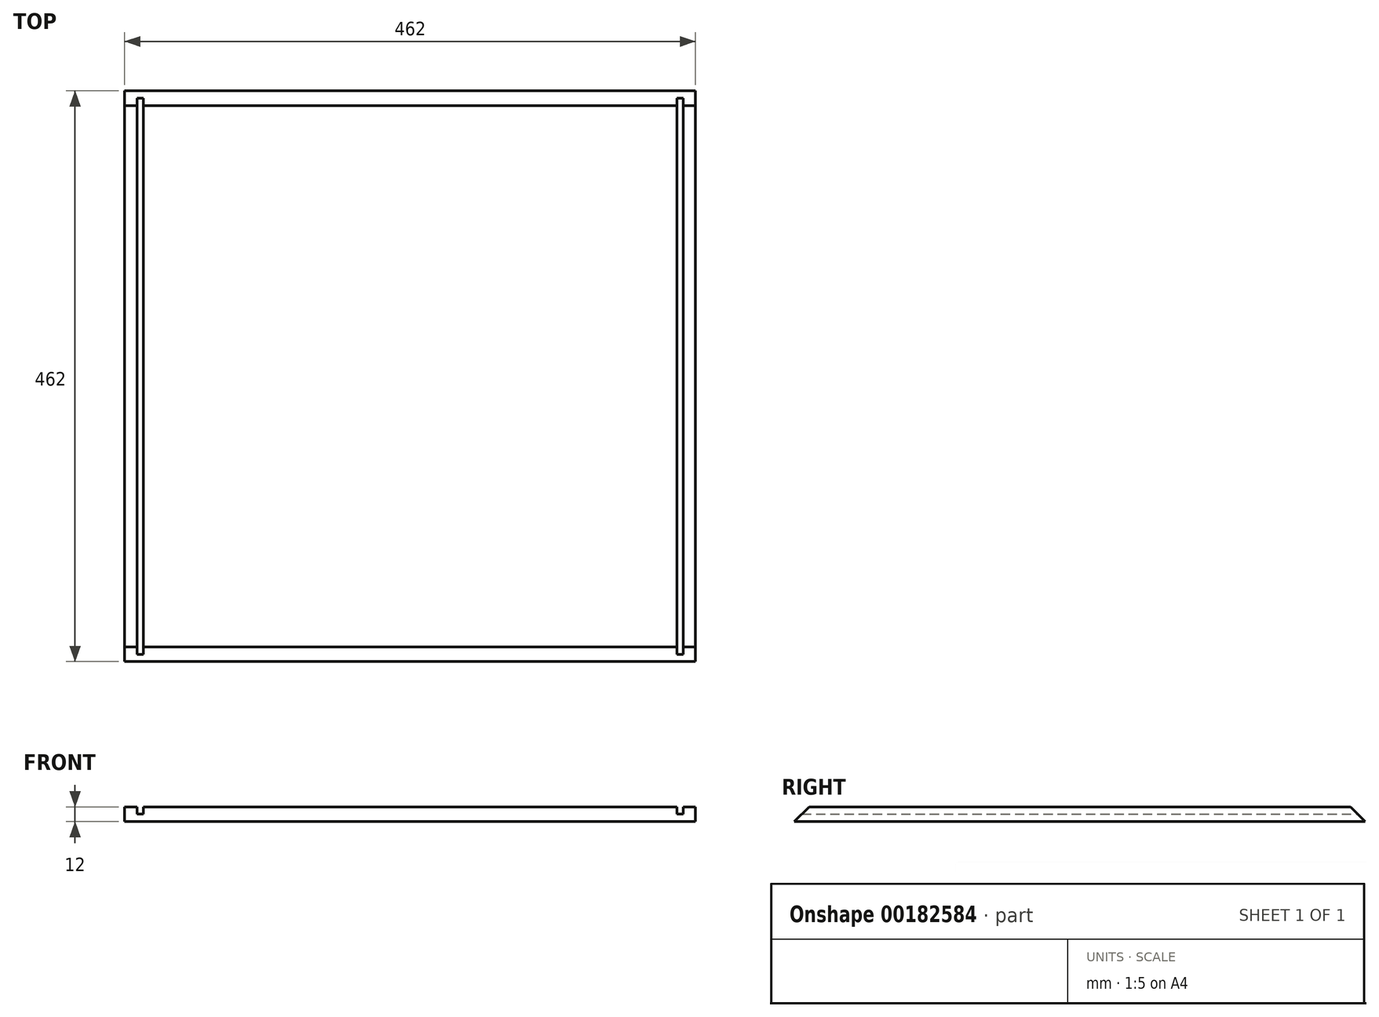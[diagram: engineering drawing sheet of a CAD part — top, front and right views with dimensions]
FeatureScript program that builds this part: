
annotation { "Feature Type Name" : "Feature", "Feature Type Description" : "" }
export const myFeature = defineFeature(function(context is Context, id is Id, definition is map)
    precondition{}
    {
        {
            var Q0;
            Q0=qCreatedBy(makeId("Top.planeOp"),FACE);
            var sketch = newSketch(context, id + "F0", { "sketchPlane" : qUnion([Q0])});
            skLineSegment(sketch, "E0.bottom", {"start": v(0, 0) * mm, "end": v(462, 0) * mm});
            skLineSegment(sketch, "E0.top", {"start": v(0, 462) * mm, "end": v(462, 462) * mm});
            skLineSegment(sketch, "E0.left", {"start": v(0, 0) * mm, "end": v(0, 462) * mm});
            skLineSegment(sketch, "E0.right", {"start": v(462, 0) * mm, "end": v(462, 462) * mm});
            skSolve(sketch);
        }
        {
            var Q0;
            Q0=qSketchRegion(id+"F0",true);
            extrude(context, id + "F1", {"entities" : qUnion([Q0]), "depth" : 12 * mm});
        }
        {
            var Q0;
            Q0=makeQuery(id+"F1.opExtrude","SWEPT_FACE",FACE,{"disambiguationData":[OSD([sQuery(id+"F0.wireOp",EDGE,"E0.right")])]});
            var sketch = newSketch(context, id + "F2", { "sketchPlane" : qUnion([Q0])});
            skLineSegment(sketch, "E1", {"start": v(0, 0) * mm, "end": v(231, 231) * mm});
            skLineSegment(sketch, "E2", {"start": v(231, 231) * mm, "end": v(462, 0) * mm});
            skLineSegment(sketch, "E3", {"start": v(462, 0) * mm, "end": v(539.72, 0) * mm});
            skLineSegment(sketch, "E4", {"start": v(539.72, 0) * mm, "end": v(539.72, 302.5) * mm});
            skLineSegment(sketch, "E5", {"start": v(539.72, 302.5) * mm, "end": v(-42.3, 283.65) * mm});
            skLineSegment(sketch, "E6", {"start": v(-42.3, 283.65) * mm, "end": v(-33.1, 0) * mm});
            skLineSegment(sketch, "E7", {"start": v(-33.1, 0) * mm, "end": v(0, 0) * mm});
            skSolve(sketch);
        }
        {
            var Q0;
            Q0=qSketchRegion(id+"F2",true);
            extrude(context, id + "F3", {"entities" : qUnion([Q0]), "operationType" : NewBodyOperationType.REMOVE, "endBound" : BoundingType.THROUGH_ALL, "oppositeDirection" : true, "depth" : 25 * mm});
        }
        {
            var Q0;
            Q0=makeQuery(id+"F1.opExtrude","CAP_FACE",FACE,{"disambiguationData":[OSD([sQuery(id+"F0.wireOp",EDGE,"E0.bottom"),sQuery(id+"F0.wireOp",EDGE,"E0.top"),sQuery(id+"F0.wireOp",EDGE,"E0.left"),sQuery(id+"F0.wireOp",EDGE,"E0.right")])],"isStart":false});
            var sketch = newSketch(context, id + "F4", { "sketchPlane" : qUnion([Q0])});
            skLineSegment(sketch, "E8.bottom", {"start": v(10, 0) * mm, "end": v(15, 0) * mm});
            skLineSegment(sketch, "E8.top", {"start": v(10, 462) * mm, "end": v(15, 462) * mm});
            skLineSegment(sketch, "E8.left", {"start": v(10, 0) * mm, "end": v(10, 462) * mm});
            skLineSegment(sketch, "E8.right", {"start": v(15, 0) * mm, "end": v(15, 462) * mm});
            skLineSegment(sketch, "E9.bottom", {"start": v(447, 0) * mm, "end": v(452, 0) * mm});
            skLineSegment(sketch, "E9.top", {"start": v(447, 462) * mm, "end": v(452, 462) * mm});
            skLineSegment(sketch, "E9.left", {"start": v(447, 0) * mm, "end": v(447, 462) * mm});
            skLineSegment(sketch, "E9.right", {"start": v(452, 0) * mm, "end": v(452, 462) * mm});
            skLineSegment(sketch, "E10.0", {"start": v(0, 462) * mm, "end": v(462, 462) * mm, "construction": true});
            skSolve(sketch);
        }
        {
            var Q0;
            Q0=qSketchRegion(id+"F4",true);
            extrude(context, id + "F5", {"entities" : qUnion([Q0]), "operationType" : NewBodyOperationType.REMOVE, "oppositeDirection" : true, "depth" : 6 * mm});
        }
    });
